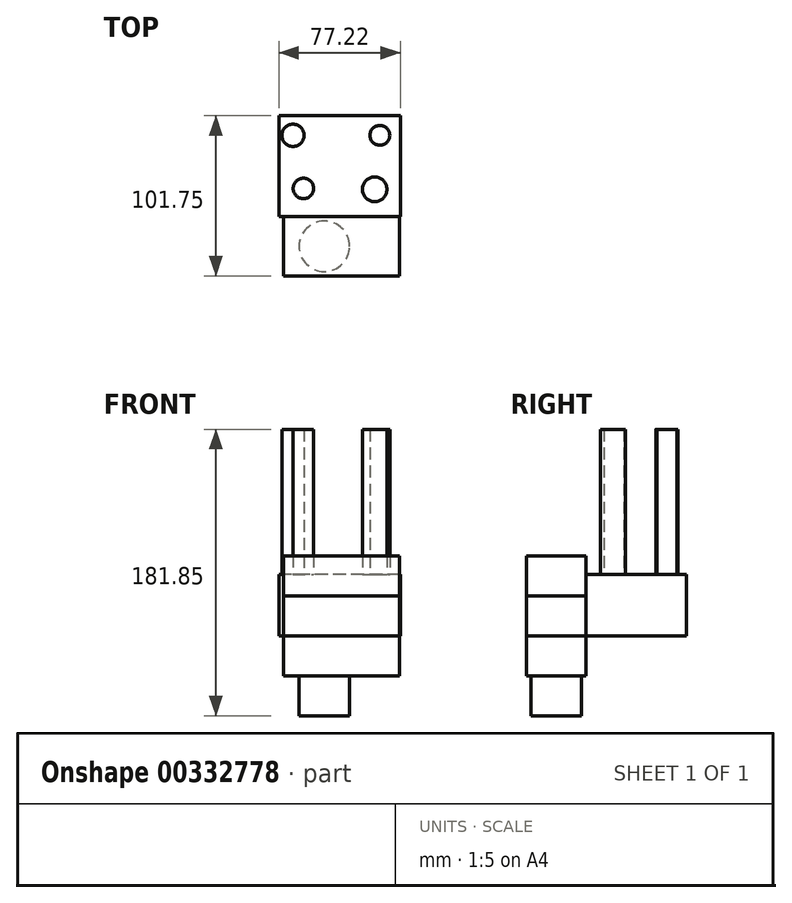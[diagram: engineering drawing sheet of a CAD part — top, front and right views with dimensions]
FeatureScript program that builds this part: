
annotation { "Feature Type Name" : "Feature", "Feature Type Description" : "" }
export const myFeature = defineFeature(function(context is Context, id is Id, definition is map)
    precondition{}
    {
        {
            var Q0;
            Q0=qCreatedBy(makeId("Right.planeOp"),FACE);
            var sketch = newSketch(context, id + "F0", { "sketchPlane" : qUnion([Q0])});
            skLineSegment(sketch, "E0.bottom", {"start": v(12.43, 52.81) * mm, "end": v(-51.64, 52.81) * mm});
            skLineSegment(sketch, "E0.top", {"start": v(12.43, 13.71) * mm, "end": v(-51.64, 13.71) * mm});
            skLineSegment(sketch, "E0.left", {"start": v(12.43, 52.81) * mm, "end": v(12.43, 13.71) * mm});
            skLineSegment(sketch, "E0.right", {"start": v(-51.64, 52.81) * mm, "end": v(-51.64, 13.71) * mm});
            skSolve(sketch);
        }
        {
            var Q0;
            Q0 = qSketchRegion(id + "F0", true);
            extrude(context, id + "F1", {"entities" : qUnion([Q0]), "depth" : 77.22 * mm});
        }
        {
            var Q0;
            Q0=makeQuery(id+"F1.opExtrude","SWEPT_FACE",FACE,{"disambiguationData":[OSD([sQuery(id+"F0.wireOp",EDGE,"E0.top")])]});
            var sketch = newSketch(context, id + "F2", { "sketchPlane" : qUnion([Q0])});
            skLineSegment(sketch, "E1.bottom", {"start": v(3.03, 51.64) * mm, "end": v(76.5, 51.64) * mm});
            skLineSegment(sketch, "E1.top", {"start": v(3.03, 89.32) * mm, "end": v(76.5, 89.32) * mm});
            skLineSegment(sketch, "E1.left", {"start": v(3.03, 51.64) * mm, "end": v(3.03, 89.32) * mm});
            skLineSegment(sketch, "E1.right", {"start": v(76.5, 51.64) * mm, "end": v(76.5, 89.32) * mm});
            skSolve(sketch);
        }
        {
            var Q0;
            Q0 = qSketchRegion(id + "F2", true);
            extrude(context, id + "F3", {"entities" : qUnion([Q0]), "depth" : 25.4 * mm});
        }
        {
            var Q0;
            Q0=makeQuery(id+"F3.opExtrude","CAP_FACE",FACE,{"disambiguationData":[OSD([sQuery(id+"F2.wireOp",EDGE,"E1.bottom"),sQuery(id+"F2.wireOp",EDGE,"E1.top"),sQuery(id+"F2.wireOp",EDGE,"E1.left"),sQuery(id+"F2.wireOp",EDGE,"E1.right")])],"isStart":true});
            extrude(context, id + "F4", {"entities" : qUnion([Q0]), "depth" : 25.4 * mm});
        }
        {
            var Q0;
            Q0=makeQuery(id+"F4.opExtrude","CAP_FACE",FACE,{"disambiguationData":[OSD([sQuery(id+"F2.wireOp",EDGE,"E1.bottom"),sQuery(id+"F2.wireOp",EDGE,"E1.top"),sQuery(id+"F2.wireOp",EDGE,"E1.left"),sQuery(id+"F2.wireOp",EDGE,"E1.right")])],"isStart":false});
            extrude(context, id + "F5", {"entities" : qUnion([Q0]), "depth" : 25.4 * mm});
        }
        {
            var Q0;
            Q0=makeQuery(id+"F1.opExtrude","SWEPT_FACE",FACE,{"disambiguationData":[OSD([sQuery(id+"F0.wireOp",EDGE,"E0.bottom")])]});
            var sketch = newSketch(context, id + "F6", { "sketchPlane" : qUnion([Q0])});
            skCircle(sketch, "E2", {"center": v(9, 0) * mm, "radius": 7.07 * mm});
            skCircle(sketch, "E3", {"center": v(64.17, 0) * mm, "radius": 6.3 * mm});
            skCircle(sketch, "E4", {"center": v(15.61, -33.72) * mm, "radius": 6.5 * mm});
            skCircle(sketch, "E5", {"center": v(60.87, -34.3) * mm, "radius": 7.84 * mm});
            skSolve(sketch);
        }
        {
            var Q0;
            Q0 = qSketchRegion(id + "F6", true);
            extrude(context, id + "F7", {"entities" : qUnion([Q0]), "operationType" : NewBodyOperationType.ADD, "depth" : 91.95 * mm});
        }
        {
            var Q0;
            Q0=makeQuery(id+"F3.opExtrude","CAP_FACE",FACE,{"disambiguationData":[OSD([sQuery(id+"F2.wireOp",EDGE,"E1.bottom"),sQuery(id+"F2.wireOp",EDGE,"E1.top"),sQuery(id+"F2.wireOp",EDGE,"E1.left"),sQuery(id+"F2.wireOp",EDGE,"E1.right")])],"isStart":false});
            var sketch = newSketch(context, id + "F8", { "sketchPlane" : qUnion([Q0])});
            skCircle(sketch, "E6", {"center": v(28.89, 70.48) * mm, "radius": 16.02 * mm});
            skPoint(sketch, "E6.centerSnap0", {"position": v(3.03, 70.48) * mm});
            skSolve(sketch);
        }
        {
            var Q0;
            Q0=makeQuery(id+"F8.imprint","IMPRINT",FACE,{"disambiguationData":[TD([[makeQuery(id+"F8.imprint","IMPRINT",EDGE,{"derivedFrom":sQuery(id+"F8.wireOp",EDGE,"E6")}),1.0]])]});
            extrude(context, id + "F9", {"entities" : qUnion([Q0]), "operationType" : NewBodyOperationType.ADD, "depth" : 25.4 * mm});
        }
    });
